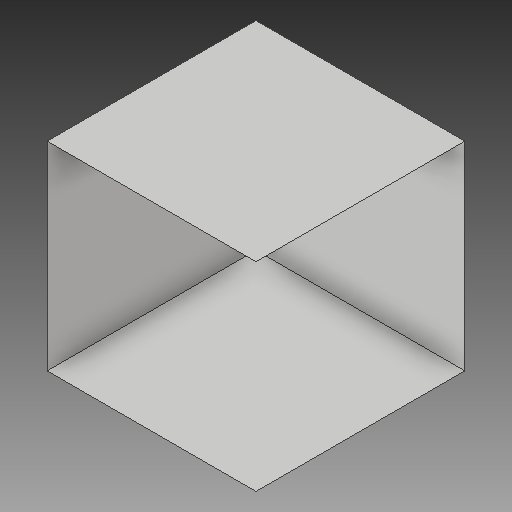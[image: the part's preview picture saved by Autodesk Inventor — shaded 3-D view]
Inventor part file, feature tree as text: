
AUTODESK INVENTOR PART (.ipt)
format: ipt  version: 2017 (Build 210142000, 142)  size: 98,304 bytes
history: native  units: in
note: dims shown in document units (in); Inventor stores cm internally (conversion verified against a paired STEP export)
features: extrude x1, other x1, sketch x1
ambient origin geometry x8: Origin, YZ Plane, XZ Plane, XY Plane, X Axis, Y Axis, Z Axis, Center Point
bodies: Solid1 (feature_tree)
feature tree (3):
  extrude  "corridor"  Depth=6.6667in
  other  "removed ends"
  sketch  "Sketch1"  dims[d0=6.6667in d1=7.0in d2=7.0in d3=0.0in]
